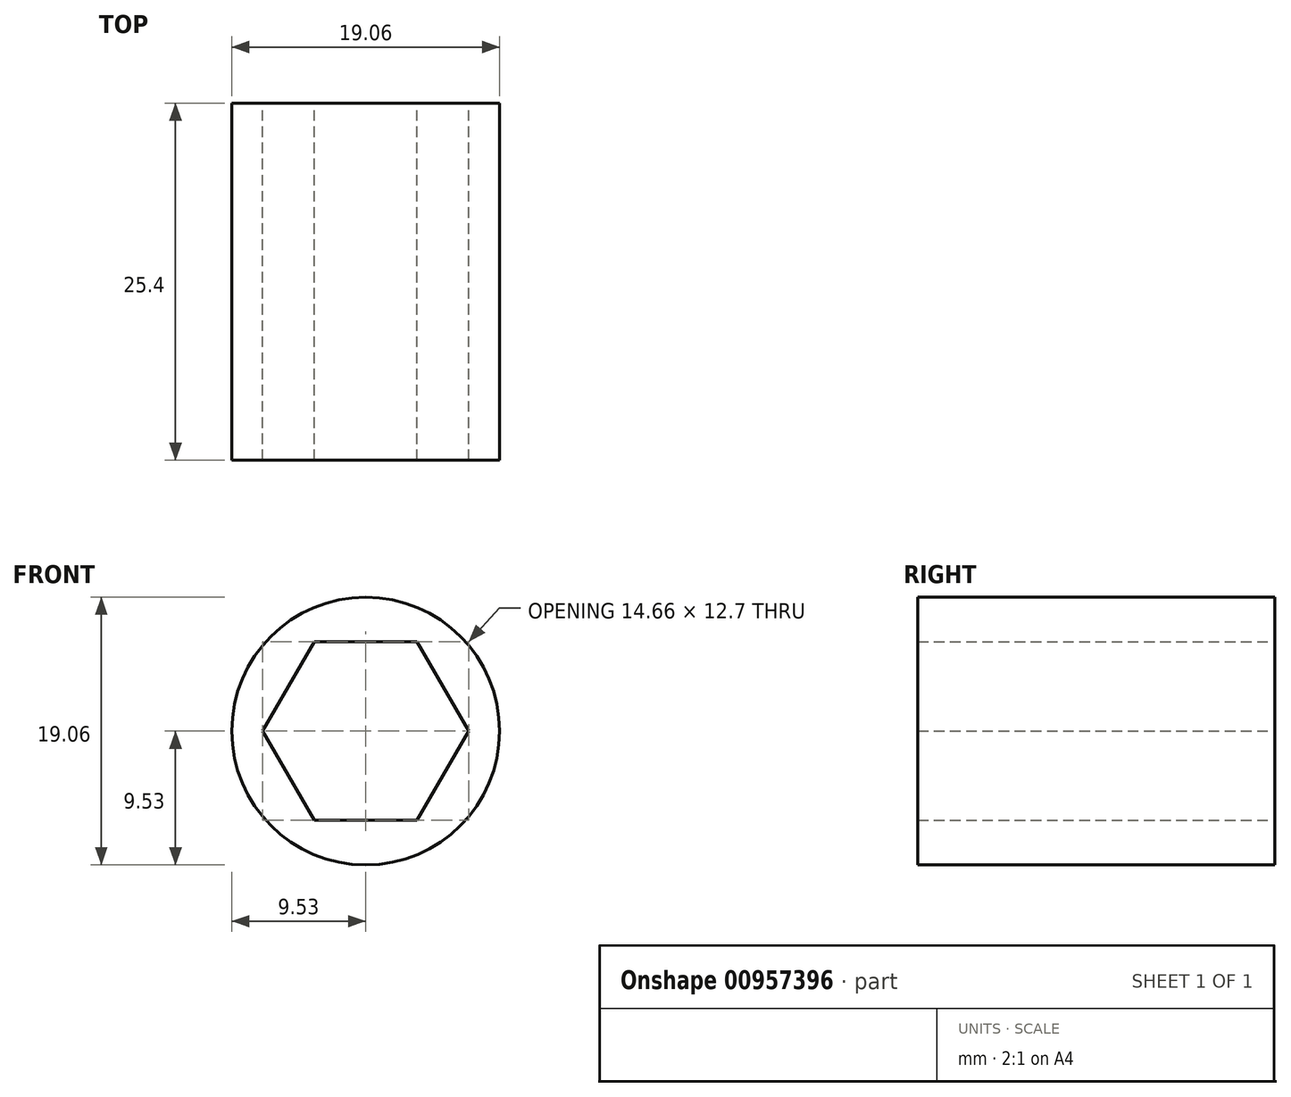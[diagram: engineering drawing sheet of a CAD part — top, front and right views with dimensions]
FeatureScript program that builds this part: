
annotation { "Feature Type Name" : "Feature", "Feature Type Description" : "" }
export const myFeature = defineFeature(function(context is Context, id is Id, definition is map)
    precondition{}
    {
        {
            var Q0;
            Q0=qCreatedBy(makeId("Front.planeOp"),FACE);
            var sketch = newSketch(context, id + "F0", { "sketchPlane" : qUnion([Q0])});
            skCircle(sketch, "E0", {"center": v(0, 0) * mm, "radius": 9.53 * mm});
            skCircle(sketch, "E1.cCircle", {"center": v(0, 0) * mm, "radius": 6.35 * mm, "construction": true});
            skLineSegment(sketch, "E1.0", {"start": v(-3.67, 6.35) * mm, "end": v(3.67, 6.35) * mm});
            skLineSegment(sketch, "E1.1", {"start": v(3.67, 6.35) * mm, "end": v(7.33, 0) * mm});
            skLineSegment(sketch, "E1.2", {"start": v(7.33, 0) * mm, "end": v(3.67, -6.35) * mm});
            skLineSegment(sketch, "E1.3", {"start": v(3.67, -6.35) * mm, "end": v(-3.67, -6.35) * mm});
            skLineSegment(sketch, "E1.4", {"start": v(-3.67, -6.35) * mm, "end": v(-7.33, 0) * mm});
            skLineSegment(sketch, "E1.5", {"start": v(-7.33, 0) * mm, "end": v(-3.67, 6.35) * mm});
            skPoint(sketch, "E1.0.midPoint", {"position": v(0, 6.35) * mm});
            skSolve(sketch);
        }
        {
            var Q0;
            Q0 = qSketchRegion(id + "F0", true);
            extrude(context, id + "F1", {"entities" : qUnion([Q0]), "depth" : 25.4 * mm, "offsetDistance" : 25.4 * mm});
        }
    });
